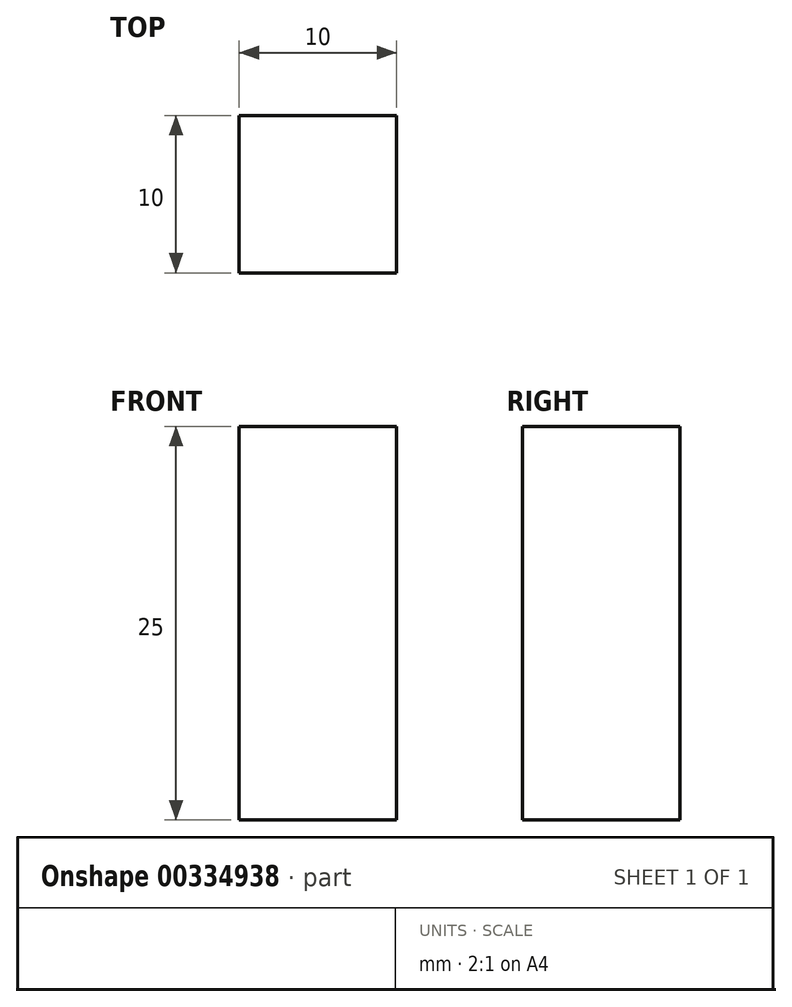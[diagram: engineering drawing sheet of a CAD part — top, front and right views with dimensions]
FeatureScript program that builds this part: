
annotation { "Feature Type Name" : "Feature", "Feature Type Description" : "" }
export const myFeature = defineFeature(function(context is Context, id is Id, definition is map)
    precondition{}
    {
        {
            var Q0;
            Q0=qCreatedBy(makeId("Top.planeOp"),FACE);
            var sketch = newSketch(context, id + "F0", { "sketchPlane" : qUnion([Q0])});
            skLineSegment(sketch, "E0.bottom", {"start": v(5, 5) * mm, "end": v(-5, 5) * mm});
            skLineSegment(sketch, "E0.top", {"start": v(5, -5) * mm, "end": v(-5, -5) * mm});
            skLineSegment(sketch, "E0.left", {"start": v(5, 5) * mm, "end": v(5, -5) * mm});
            skLineSegment(sketch, "E0.right", {"start": v(-5, 5) * mm, "end": v(-5, -5) * mm});
            skPoint(sketch, "E0.middle", {"position": v(0, 0) * mm});
            skSolve(sketch);
        }
        {
            var Q0;
            Q0 = qSketchRegion(id + "F0", true);
            extrude(context, id + "F1", {"entities" : qUnion([Q0]), "depth" : 25 * mm});
        }
    });
